# Revit family: RUFO2 460xWSxZ0350xx
name_source: partatom
category: Leuchten
units: mm (PartAtom-declared; Revit-internal decimal feet)

## family parameters
Basisbauteil = Fläche
Beim Laden mit Abzugskörper schneiden = Nein
Bemaßung runder Anschluss = Durchmesser verwenden
Gemeinsam genutzt = Nein
Lichtquelle = Ja
OmniClass-Nummer = 23.80.70.11
OmniClass-Titel = Luminaries for Internal Lighting
Raumberechnungspunkt = Nein
Teiletyp = Normal

## types (18) — shared parameters
Baugruppenkennzeichen = D5020200
Datei für fotometrisches Netz = RUFO2_460_Z.IES
Emissionsform beim Rendern sichtbar = Nein
Farbfilter = 16777215
Farbtemperaturverschiebung bei Dämpfen der Lampe = <Keine Auswahl>
Hersteller = RIDI Leuchten GmbH
Lampe = LED
Neigungswinkel = 90.00°
Scheinlast = 30 VA
URL = www.ridi.de
Von Kreisdurchmesser aussenden = 464 mm  [stored 1.52231 ft]
brand = RIDI
conformity mark = CE
electrical safety class = 1
height = 70 mm  [stored 0.229659 ft]
ingress protection (IP) code = IP40
length = 464 mm  [stored 1.52231 ft]
nominal frequency = 50-60Hz
nominal voltage = 230
rated input power = 30
voltage type (AC, DC, UC) = AC
width = 464 mm  [stored 1.52231 ft]
zero-valued in all types: Vorgabe-Ansicht

## per-type parameters (varying)
| type | Modell | weight |
| RUFO2 460NDWS840Z0350 | 0420869 | 2 kg |
| RUFO2 460NDWS840Z0350-RS | 0420869//396 | 2.05 kg |
| RUFO2 460NDWS840Z0350-2K | 0420870 | 2.15 kg |
| RUFO2 460NDWS830Z0350 | 0420875 | 2 kg |
| RUFO2 460NDWS830Z0350-RS | 0420875//396 | 2.05 kg |
| RUFO2 460NDWS830Z0350-2K | 0420876 | 2.15 kg |
| RUFO2 460NDWS840Z0350-IK | 0420881 | 2 kg |
| RUFO2 460NDWS840Z0350-IK-EDS3 | 0420881//377 | 2.5 kg |
| RUFO2 460NDWS840Z0350-IK-RS | 0420881//396 | 2.05 kg |
| RUFO2 460NDWS840Z0350-IK-2K | 0420882 | 2.15 kg |
| RUFO2 460NDWS830Z0350-IK | 0420887 | 2 kg |
| RUFO2 460NDWS830Z0350-IK-EDS3 | 0420887//377 | 2.5 kg |
| RUFO2 460NDWS830Z0350-IK-RS | 0420887//396 | 2.05 kg |
| RUFO2 460NDWS830Z0350-IK-2K | 0420888 | 2.15 kg |
| RUFO2 460DAWS840Z0350 | 0430869 | 2.05 kg |
| RUFO2 460DAWS830Z0350 | 0430875 | 2.05 kg |
| RUFO2 460DAWS840Z0350-IK | 0430881 | 2.05 kg |
| RUFO2 460DAWS830Z0350-IK | 0430887 | 2.05 kg |

note: column(s) folded — value = type name in every type: product name

note: [stored X ft] marks values corroborated as IEEE doubles in the binary element streams (Revit-internal decimal feet)
